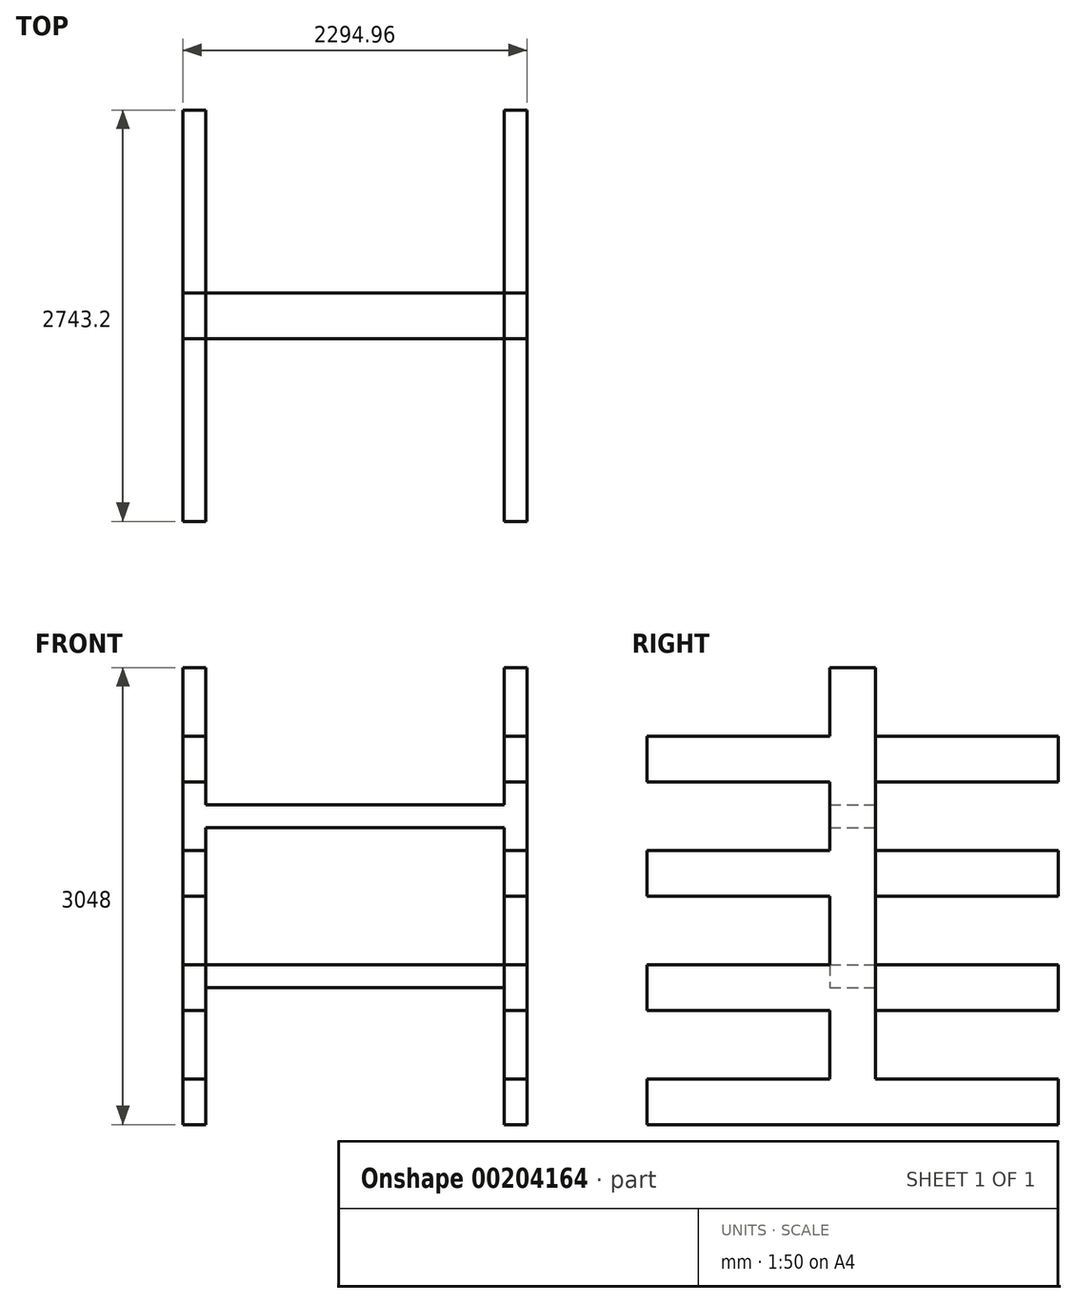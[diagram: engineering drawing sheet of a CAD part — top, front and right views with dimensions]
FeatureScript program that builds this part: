
annotation { "Feature Type Name" : "Feature", "Feature Type Description" : "" }
export const myFeature = defineFeature(function(context is Context, id is Id, definition is map)
    precondition{}
    {
        {
            var Q0;
            Q0=qCreatedBy(makeId("Front.planeOp"),FACE);
            var sketch = newSketch(context, id + "F0", { "sketchPlane" : qUnion([Q0])});
            skLineSegment(sketch, "E0", {"start": v(0, 0) * mm, "end": v(0, 3048) * mm});
            skLineSegment(sketch, "E1", {"start": v(2294.96, 3048) * mm, "end": v(2294.96, 0) * mm});
            skLineSegment(sketch, "E2", {"start": v(2294.96, 0) * mm, "end": v(2142.56, 0) * mm});
            skLineSegment(sketch, "E3", {"start": v(152.4, 0) * mm, "end": v(0, 0) * mm});
            skLineSegment(sketch, "E4", {"start": v(0, 3048) * mm, "end": v(152.4, 3048) * mm});
            skLineSegment(sketch, "E5", {"start": v(152.4, 3048) * mm, "end": v(152.4, 2133.6) * mm});
            skLineSegment(sketch, "E6", {"start": v(152.4, 2133.6) * mm, "end": v(2142.56, 2133.6) * mm});
            skLineSegment(sketch, "E7", {"start": v(2142.56, 2133.6) * mm, "end": v(2142.56, 3048) * mm});
            skLineSegment(sketch, "E8", {"start": v(2142.56, 3048) * mm, "end": v(2294.96, 3048) * mm});
            skLineSegment(sketch, "E9", {"start": v(152.4, 0) * mm, "end": v(152.4, 914.4) * mm});
            skLineSegment(sketch, "E10", {"start": v(152.4, 914.4) * mm, "end": v(2142.56, 914.4) * mm});
            skLineSegment(sketch, "E11", {"start": v(2142.56, 914.4) * mm, "end": v(2142.56, 0) * mm});
            skLineSegment(sketch, "E12.bottom", {"start": v(152.4, 1981.2) * mm, "end": v(2142.56, 1981.2) * mm});
            skLineSegment(sketch, "E12.top", {"start": v(152.4, 1066.8) * mm, "end": v(2142.56, 1066.8) * mm});
            skLineSegment(sketch, "E12.left", {"start": v(152.4, 1981.2) * mm, "end": v(152.4, 1066.8) * mm});
            skLineSegment(sketch, "E12.right", {"start": v(2142.56, 1981.2) * mm, "end": v(2142.56, 1066.8) * mm});
            skSolve(sketch);
        }
        {
            var Q0;
            Q0=makeQuery(id+"F0.imprint","IMPRINT",FACE,{"disambiguationData":[TD([[makeQuery(id+"F0.imprint","IMPRINT",EDGE,{"derivedFrom":sQuery(id+"F0.wireOp",EDGE,"E0")}),-1.0]])]});
            extrude(context, id + "F1", {"entities" : qUnion([Q0]), "depth" : 304.8 * mm});
        }
        {
            var Q0;
            Q0=makeQuery(id+"F1.opExtrude","CAP_FACE",FACE,{"disambiguationData":[OSD([sQuery(id+"F0.wireOp",EDGE,"E0"),sQuery(id+"F0.wireOp",EDGE,"E1"),sQuery(id+"F0.wireOp",EDGE,"E2"),sQuery(id+"F0.wireOp",EDGE,"E3"),sQuery(id+"F0.wireOp",EDGE,"E4"),sQuery(id+"F0.wireOp",EDGE,"E5"),sQuery(id+"F0.wireOp",EDGE,"E6"),sQuery(id+"F0.wireOp",EDGE,"E7"),sQuery(id+"F0.wireOp",EDGE,"E8"),sQuery(id+"F0.wireOp",EDGE,"E9"),sQuery(id+"F0.wireOp",EDGE,"E10"),sQuery(id+"F0.wireOp",EDGE,"E11"),sQuery(id+"F0.wireOp",EDGE,"E12.bottom"),sQuery(id+"F0.wireOp",EDGE,"E12.top"),sQuery(id+"F0.wireOp",EDGE,"E12.left"),sQuery(id+"F0.wireOp",EDGE,"E12.right")])],"isStart":false});
            var sketch = newSketch(context, id + "F2", { "sketchPlane" : qUnion([Q0])});
            skLineSegment(sketch, "E13.bottom", {"start": v(0, 0) * mm, "end": v(152.4, 0) * mm});
            skLineSegment(sketch, "E13.top", {"start": v(0, 304.8) * mm, "end": v(152.4, 304.8) * mm});
            skLineSegment(sketch, "E13.left", {"start": v(0, 0) * mm, "end": v(0, 304.8) * mm});
            skLineSegment(sketch, "E13.right", {"start": v(152.4, 0) * mm, "end": v(152.4, 304.8) * mm});
            skLineSegment(sketch, "E14.bottom", {"start": v(0, 1524) * mm, "end": v(152.4, 1524) * mm});
            skLineSegment(sketch, "E14.top", {"start": v(0, 1828.8) * mm, "end": v(152.4, 1828.8) * mm});
            skLineSegment(sketch, "E14.left", {"start": v(0, 1524) * mm, "end": v(0, 1828.8) * mm});
            skLineSegment(sketch, "E14.right", {"start": v(152.4, 1524) * mm, "end": v(152.4, 1828.8) * mm});
            skLineSegment(sketch, "E15.bottom", {"start": v(0, 762) * mm, "end": v(152.4, 762) * mm});
            skLineSegment(sketch, "E15.top", {"start": v(0, 1066.8) * mm, "end": v(152.4, 1066.8) * mm});
            skLineSegment(sketch, "E15.left", {"start": v(0, 762) * mm, "end": v(0, 1066.8) * mm});
            skLineSegment(sketch, "E15.right", {"start": v(152.4, 762) * mm, "end": v(152.4, 1066.8) * mm});
            skLineSegment(sketch, "E16.bottom", {"start": v(0, 2286) * mm, "end": v(152.4, 2286) * mm});
            skLineSegment(sketch, "E16.top", {"start": v(0, 2590.8) * mm, "end": v(152.4, 2590.8) * mm});
            skLineSegment(sketch, "E16.left", {"start": v(0, 2286) * mm, "end": v(0, 2590.8) * mm});
            skLineSegment(sketch, "E16.right", {"start": v(152.4, 2286) * mm, "end": v(152.4, 2590.8) * mm});
            skLineSegment(sketch, "E17.bottom", {"start": v(2142.56, 0) * mm, "end": v(2294.96, 0) * mm});
            skLineSegment(sketch, "E17.top", {"start": v(2142.56, 304.8) * mm, "end": v(2294.96, 304.8) * mm});
            skLineSegment(sketch, "E17.left", {"start": v(2142.56, 0) * mm, "end": v(2142.56, 304.8) * mm});
            skLineSegment(sketch, "E17.right", {"start": v(2294.96, 0) * mm, "end": v(2294.96, 304.8) * mm});
            skLineSegment(sketch, "E18.bottom", {"start": v(2142.56, 1524) * mm, "end": v(2294.96, 1524) * mm});
            skLineSegment(sketch, "E18.top", {"start": v(2142.56, 1828.8) * mm, "end": v(2294.96, 1828.8) * mm});
            skLineSegment(sketch, "E18.left", {"start": v(2142.56, 1524) * mm, "end": v(2142.56, 1828.8) * mm});
            skLineSegment(sketch, "E18.right", {"start": v(2294.96, 1524) * mm, "end": v(2294.96, 1828.8) * mm});
            skLineSegment(sketch, "E19.bottom", {"start": v(2142.56, 762) * mm, "end": v(2294.96, 762) * mm});
            skLineSegment(sketch, "E19.top", {"start": v(2142.56, 1066.8) * mm, "end": v(2294.96, 1066.8) * mm});
            skLineSegment(sketch, "E19.left", {"start": v(2142.56, 762) * mm, "end": v(2142.56, 1066.8) * mm});
            skLineSegment(sketch, "E19.right", {"start": v(2294.96, 762) * mm, "end": v(2294.96, 1066.8) * mm});
            skLineSegment(sketch, "E20.bottom", {"start": v(2142.56, 2286) * mm, "end": v(2294.96, 2286) * mm});
            skLineSegment(sketch, "E20.top", {"start": v(2142.56, 2590.8) * mm, "end": v(2294.96, 2590.8) * mm});
            skLineSegment(sketch, "E20.left", {"start": v(2142.56, 2286) * mm, "end": v(2142.56, 2590.8) * mm});
            skLineSegment(sketch, "E20.right", {"start": v(2294.96, 2286) * mm, "end": v(2294.96, 2590.8) * mm});
            skSolve(sketch);
        }
        {
            var Q0;
            Q0 = qSketchRegion(id + "F2", true);
            extrude(context, id + "F3", {"entities" : qUnion([Q0]), "operationType" : NewBodyOperationType.ADD, "depth" : 1219.2 * mm});
        }
        {
            var Q0;
            Q0=makeQuery(id+"F1.opExtrude","CAP_FACE",FACE,{"disambiguationData":[OSD([sQuery(id+"F0.wireOp",EDGE,"E0"),sQuery(id+"F0.wireOp",EDGE,"E1"),sQuery(id+"F0.wireOp",EDGE,"E2"),sQuery(id+"F0.wireOp",EDGE,"E3"),sQuery(id+"F0.wireOp",EDGE,"E4"),sQuery(id+"F0.wireOp",EDGE,"E5"),sQuery(id+"F0.wireOp",EDGE,"E6"),sQuery(id+"F0.wireOp",EDGE,"E7"),sQuery(id+"F0.wireOp",EDGE,"E8"),sQuery(id+"F0.wireOp",EDGE,"E9"),sQuery(id+"F0.wireOp",EDGE,"E10"),sQuery(id+"F0.wireOp",EDGE,"E11"),sQuery(id+"F0.wireOp",EDGE,"E12.bottom"),sQuery(id+"F0.wireOp",EDGE,"E12.top"),sQuery(id+"F0.wireOp",EDGE,"E12.left"),sQuery(id+"F0.wireOp",EDGE,"E12.right")])],"isStart":true});
            var sketch = newSketch(context, id + "F4", { "sketchPlane" : qUnion([Q0])});
            skLineSegment(sketch, "E21.bottom", {"start": v(-2294.96, 0.03) * mm, "end": v(-2142.56, 0.03) * mm});
            skLineSegment(sketch, "E21.top", {"start": v(-2294.96, 304.83) * mm, "end": v(-2142.56, 304.83) * mm});
            skLineSegment(sketch, "E21.left", {"start": v(-2294.96, 0.03) * mm, "end": v(-2294.96, 304.83) * mm});
            skLineSegment(sketch, "E21.right", {"start": v(-2142.56, 0.03) * mm, "end": v(-2142.56, 304.83) * mm});
            skLineSegment(sketch, "E22.bottom", {"start": v(-2294.96, 1524.03) * mm, "end": v(-2142.56, 1524.03) * mm});
            skLineSegment(sketch, "E22.top", {"start": v(-2294.96, 1828.83) * mm, "end": v(-2142.56, 1828.83) * mm});
            skLineSegment(sketch, "E22.left", {"start": v(-2294.96, 1524.03) * mm, "end": v(-2294.96, 1828.83) * mm});
            skLineSegment(sketch, "E22.right", {"start": v(-2142.56, 1524.03) * mm, "end": v(-2142.56, 1828.83) * mm});
            skLineSegment(sketch, "E23.bottom", {"start": v(-2294.96, 762.03) * mm, "end": v(-2142.56, 762.03) * mm});
            skLineSegment(sketch, "E23.top", {"start": v(-2294.96, 1066.83) * mm, "end": v(-2142.56, 1066.83) * mm});
            skLineSegment(sketch, "E23.left", {"start": v(-2294.96, 762.03) * mm, "end": v(-2294.96, 1066.83) * mm});
            skLineSegment(sketch, "E23.right", {"start": v(-2142.56, 762.03) * mm, "end": v(-2142.56, 1066.83) * mm});
            skLineSegment(sketch, "E24.bottom", {"start": v(-2294.96, 2286.03) * mm, "end": v(-2142.56, 2286.03) * mm});
            skLineSegment(sketch, "E24.top", {"start": v(-2294.96, 2590.83) * mm, "end": v(-2142.56, 2590.83) * mm});
            skLineSegment(sketch, "E24.left", {"start": v(-2294.96, 2286.03) * mm, "end": v(-2294.96, 2590.83) * mm});
            skLineSegment(sketch, "E24.right", {"start": v(-2142.56, 2286.03) * mm, "end": v(-2142.56, 2590.83) * mm});
            skLineSegment(sketch, "E25.bottom", {"start": v(-152.4, 0.03) * mm, "end": v(0, 0.03) * mm});
            skLineSegment(sketch, "E25.top", {"start": v(-152.4, 304.83) * mm, "end": v(0, 304.83) * mm});
            skLineSegment(sketch, "E25.left", {"start": v(-152.4, 0.03) * mm, "end": v(-152.4, 304.83) * mm});
            skLineSegment(sketch, "E25.right", {"start": v(0, 0.03) * mm, "end": v(0, 304.83) * mm});
            skLineSegment(sketch, "E26.bottom", {"start": v(-152.4, 1524.03) * mm, "end": v(0, 1524.03) * mm});
            skLineSegment(sketch, "E26.top", {"start": v(-152.4, 1828.83) * mm, "end": v(0, 1828.83) * mm});
            skLineSegment(sketch, "E26.left", {"start": v(-152.4, 1524.03) * mm, "end": v(-152.4, 1828.83) * mm});
            skLineSegment(sketch, "E26.right", {"start": v(0, 1524.03) * mm, "end": v(0, 1828.83) * mm});
            skLineSegment(sketch, "E27.bottom", {"start": v(-152.4, 762.03) * mm, "end": v(0, 762.03) * mm});
            skLineSegment(sketch, "E27.top", {"start": v(-152.4, 1066.83) * mm, "end": v(0, 1066.83) * mm});
            skLineSegment(sketch, "E27.left", {"start": v(-152.4, 762.03) * mm, "end": v(-152.4, 1066.83) * mm});
            skLineSegment(sketch, "E27.right", {"start": v(0, 762.03) * mm, "end": v(0, 1066.83) * mm});
            skLineSegment(sketch, "E28.bottom", {"start": v(-152.4, 2286.03) * mm, "end": v(0, 2286.03) * mm});
            skLineSegment(sketch, "E28.top", {"start": v(-152.4, 2590.83) * mm, "end": v(0, 2590.83) * mm});
            skLineSegment(sketch, "E28.left", {"start": v(-152.4, 2286.03) * mm, "end": v(-152.4, 2590.83) * mm});
            skLineSegment(sketch, "E28.right", {"start": v(0, 2286.03) * mm, "end": v(0, 2590.83) * mm});
            skSolve(sketch);
        }
        {
            var Q0;
            Q0 = qSketchRegion(id + "F4", true);
            extrude(context, id + "F5", {"entities" : qUnion([Q0]), "operationType" : NewBodyOperationType.ADD, "depth" : 1219.2 * mm});
        }
    });
